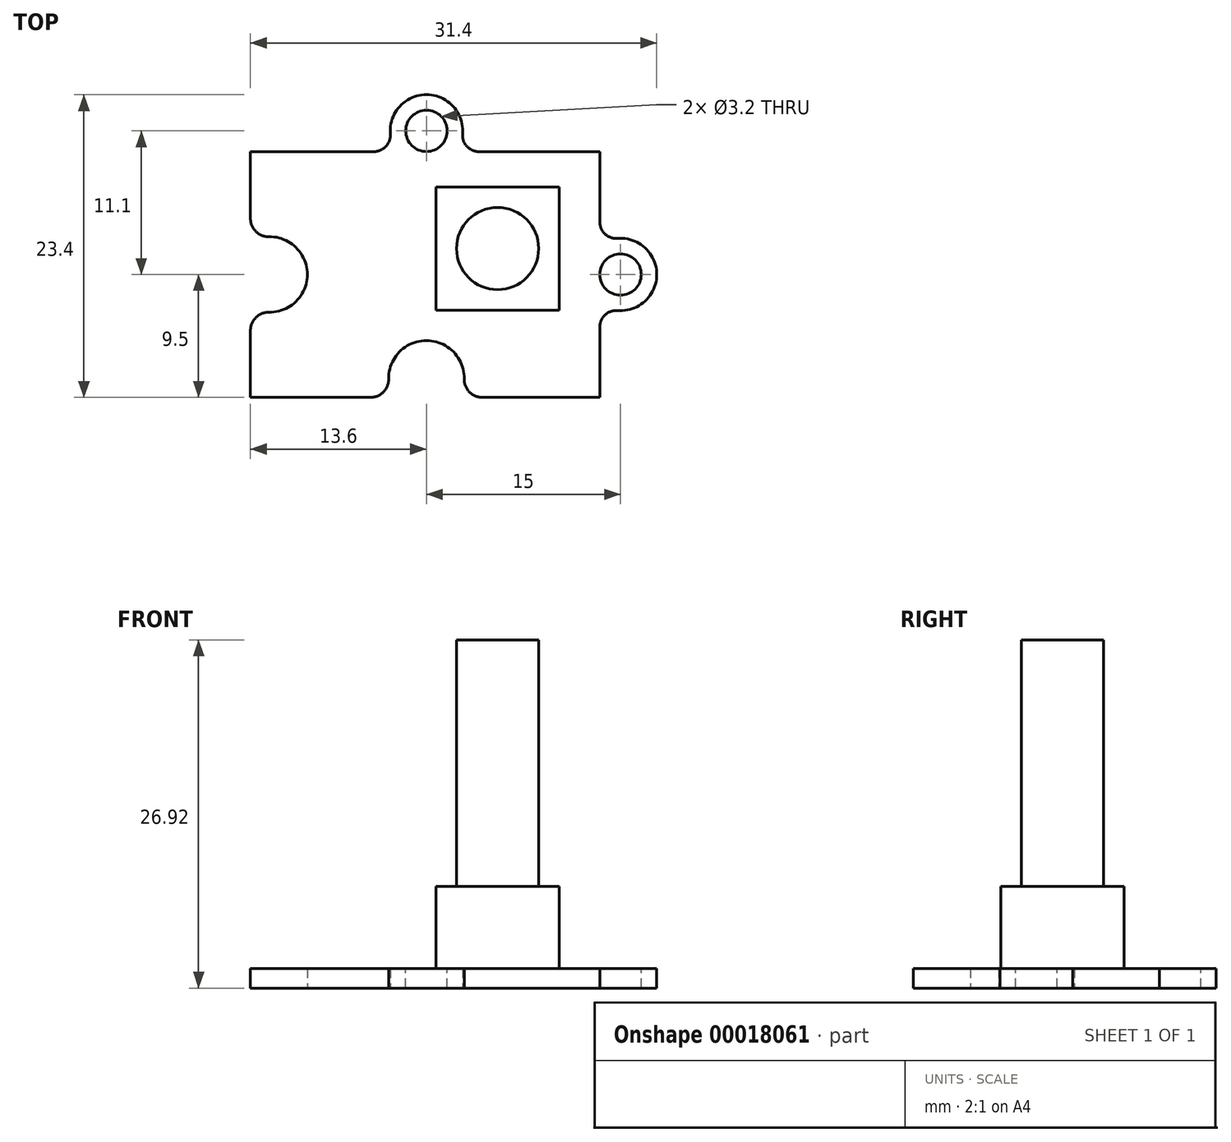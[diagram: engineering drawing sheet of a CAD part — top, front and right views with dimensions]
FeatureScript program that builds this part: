
annotation { "Feature Type Name" : "Feature", "Feature Type Description" : "" }
export const myFeature = defineFeature(function(context is Context, id is Id, definition is map)
    precondition{}
    {
        {
            var Q0;
            Q0=qCreatedBy(makeId("Top.planeOp"),FACE);
            var sketch = newSketch(context, id + "F0", { "sketchPlane" : qUnion([Q0])});
            skLineSegment(sketch, "E0.bottom", {"start": v(0, 0) * mm, "end": v(9.28, 0) * mm});
            skLineSegment(sketch, "E0.top", {"start": v(0, 19) * mm, "end": v(9.54, 19) * mm});
            skLineSegment(sketch, "E0.left", {"start": v(0, 0) * mm, "end": v(0, 5.18) * mm});
            skLineSegment(sketch, "E0.right", {"start": v(27, 0) * mm, "end": v(27, 5.44) * mm});
            skLineSegment(sketch, "E1", {"start": v(-7.73, 9.5) * mm, "end": v(31.46, 9.5) * mm, "construction": true});
            skPoint(sketch, "E2", {"position": v(0, 9.5) * mm});
            skPoint(sketch, "E3", {"position": v(27, 9.5) * mm});
            skArc(sketch, "E4", {"start": v(1.42, 6.58) * mm, "mid": v(4.4, 9.5) * mm, "end": v(1.42, 12.42) * mm});
            skArc(sketch, "E5", {"start": v(28.37, 6.7) * mm, "mid": v(31.4, 9.5) * mm, "end": v(28.37, 12.3) * mm});
            skLineSegment(sketch, "E6", {"start": v(13.6, 24.26) * mm, "end": v(13.6, -6.17) * mm, "construction": true});
            skArc(sketch, "E7", {"start": v(16.4, 20.37) * mm, "mid": v(13.6, 23.4) * mm, "end": v(10.8, 20.37) * mm});
            skArc(sketch, "E8", {"start": v(16.52, 1.42) * mm, "mid": v(13.6, 4.4) * mm, "end": v(10.68, 1.42) * mm});
            skCircle(sketch, "E9", {"center": v(13.6, 20.6) * mm, "radius": 1.6 * mm, "construction": true});
            skCircle(sketch, "E10", {"center": v(28.6, 9.5) * mm, "radius": 1.6 * mm, "construction": true});
            skLineSegment(sketch, "E11.trimOffspring", {"start": v(0, 13.82) * mm, "end": v(0, 19) * mm});
            skLineSegment(sketch, "E12.trimOffspring", {"start": v(27, 13.56) * mm, "end": v(27, 19) * mm});
            skLineSegment(sketch, "E13.trimOffspring", {"start": v(17.66, 19) * mm, "end": v(27, 19) * mm});
            skLineSegment(sketch, "E14.trimOffspring", {"start": v(17.92, 0) * mm, "end": v(27, 0) * mm});
            skPoint(sketch, "E15.visualSharp", {"position": v(11.3, 19) * mm});
            skArc(sketch, "E15.filletArc", {"start": v(9.54, 19) * mm, "mid": v(10.48, 19.4) * mm, "end": v(10.8, 20.37) * mm});
            skPoint(sketch, "E16.visualSharp", {"position": v(15.9, 19) * mm});
            skArc(sketch, "E16.filletArc", {"start": v(16.4, 20.37) * mm, "mid": v(16.72, 19.4) * mm, "end": v(17.66, 19) * mm});
            skPoint(sketch, "E17.visualSharp", {"position": v(11.08, 0) * mm});
            skArc(sketch, "E17.filletArc", {"start": v(9.28, 0) * mm, "mid": v(10.28, 0.42) * mm, "end": v(10.68, 1.42) * mm});
            skPoint(sketch, "E18.visualSharp", {"position": v(16.12, 0) * mm});
            skArc(sketch, "E18.filletArc", {"start": v(16.52, 1.42) * mm, "mid": v(16.92, 0.42) * mm, "end": v(17.92, 0) * mm});
            skPoint(sketch, "E19.visualSharp", {"position": v(27, 11.8) * mm});
            skArc(sketch, "E19.filletArc", {"start": v(27, 13.56) * mm, "mid": v(27.4, 12.62) * mm, "end": v(28.37, 12.3) * mm});
            skPoint(sketch, "E20.visualSharp", {"position": v(27, 7.2) * mm});
            skArc(sketch, "E20.filletArc", {"start": v(28.37, 6.7) * mm, "mid": v(27.4, 6.38) * mm, "end": v(27, 5.44) * mm});
            skPoint(sketch, "E21.visualSharp", {"position": v(0, 12.02) * mm});
            skArc(sketch, "E21.filletArc", {"start": v(0, 13.82) * mm, "mid": v(0.42, 12.82) * mm, "end": v(1.42, 12.42) * mm});
            skPoint(sketch, "E22.visualSharp", {"position": v(0, 6.98) * mm});
            skArc(sketch, "E22.filletArc", {"start": v(1.42, 6.58) * mm, "mid": v(0.42, 6.18) * mm, "end": v(0, 5.18) * mm});
            skSolve(sketch);
        }
        {
            var Q0;
            Q0 = qSketchRegion(id + "F0", true);
            extrude(context, id + "F1", {"entities" : qUnion([Q0]), "depth" : 1.52 * mm});
        }
        {
            var Q0;
            Q0=makeQuery(id+"F1.opExtrude","CAP_FACE",FACE,{"disambiguationData":[OSD([sQuery(id+"F0.wireOp",EDGE,"E0.bottom"),sQuery(id+"F0.wireOp",EDGE,"E0.top"),sQuery(id+"F0.wireOp",EDGE,"E0.left"),sQuery(id+"F0.wireOp",EDGE,"E0.right"),sQuery(id+"F0.wireOp",EDGE,"E4"),sQuery(id+"F0.wireOp",EDGE,"E5"),sQuery(id+"F0.wireOp",EDGE,"E7"),sQuery(id+"F0.wireOp",EDGE,"E8"),sQuery(id+"F0.wireOp",EDGE,"E11.trimOffspring"),sQuery(id+"F0.wireOp",EDGE,"E12.trimOffspring"),sQuery(id+"F0.wireOp",EDGE,"E13.trimOffspring"),sQuery(id+"F0.wireOp",EDGE,"E14.trimOffspring"),sQuery(id+"F0.wireOp",EDGE,"E15.filletArc"),sQuery(id+"F0.wireOp",EDGE,"E16.filletArc"),sQuery(id+"F0.wireOp",EDGE,"E17.filletArc"),sQuery(id+"F0.wireOp",EDGE,"E18.filletArc"),sQuery(id+"F0.wireOp",EDGE,"E19.filletArc"),sQuery(id+"F0.wireOp",EDGE,"E20.filletArc"),sQuery(id+"F0.wireOp",EDGE,"E21.filletArc"),sQuery(id+"F0.wireOp",EDGE,"E22.filletArc")])],"isStart":false});
            var sketch = newSketch(context, id + "F2", { "sketchPlane" : qUnion([Q0])});
            skCircle(sketch, "E23", {"center": v(19.1, 11.5) * mm, "radius": 3.05 * mm, "construction": true});
            skPoint(sketch, "E24", {"position": v(28.6, 9.5) * mm});
            skPoint(sketch, "E25", {"position": v(13.6, 20.6) * mm});
            skLineSegment(sketch, "E26.bottom", {"start": v(14.34, 16.27) * mm, "end": v(23.86, 16.27) * mm});
            skLineSegment(sketch, "E26.top", {"start": v(14.34, 6.74) * mm, "end": v(23.86, 6.74) * mm});
            skLineSegment(sketch, "E26.left", {"start": v(14.34, 16.27) * mm, "end": v(14.34, 6.74) * mm});
            skLineSegment(sketch, "E26.right", {"start": v(23.86, 16.27) * mm, "end": v(23.86, 6.74) * mm});
            skSolve(sketch);
        }
        {
            var Q0;
            Q0 = qSketchRegion(id + "F2", true);
            extrude(context, id + "F3", {"entities" : qUnion([Q0]), "operationType" : NewBodyOperationType.ADD, "depth" : 6.35 * mm});
        }
        {
            var Q0;
            Q0=makeQuery(id+"F3.opExtrude","CAP_FACE",FACE,{"disambiguationData":[OSD([sQuery(id+"F2.wireOp",EDGE,"E26.bottom"),sQuery(id+"F2.wireOp",EDGE,"E26.top"),sQuery(id+"F2.wireOp",EDGE,"E26.left"),sQuery(id+"F2.wireOp",EDGE,"E26.right")])],"isStart":false});
            var sketch = newSketch(context, id + "F4", { "sketchPlane" : qUnion([Q0])});
            skPoint(sketch, "E27.0", {"position": v(19.1, 11.5) * mm});
            skCircle(sketch, "E28", {"center": v(19.1, 11.5) * mm, "radius": 3.18 * mm});
            skSolve(sketch);
        }
        {
            var Q0;
            Q0 = qSketchRegion(id + "F4", true);
            extrude(context, id + "F5", {"entities" : qUnion([Q0]), "operationType" : NewBodyOperationType.ADD, "depth" : 19.05 * mm});
        }
        {
            var Q0;
            Q0=makeQuery(id+"F2.imprint","IMPRINT",FACE,{"disambiguationData":[TD([[makeQuery(id+"F2.imprint","IMPRINT",EDGE,{"derivedFrom":sQuery(id+"F2.wireOp",EDGE,"E26.bottom")}),1.0]])]});
            var sketch = newSketch(context, id + "F6", { "sketchPlane" : qUnion([Q0])});
            skCircle(sketch, "E29", {"center": v(13.6, 20.6) * mm, "radius": 1.6 * mm});
            skCircle(sketch, "E30", {"center": v(28.6, 9.5) * mm, "radius": 1.6 * mm});
            skSolve(sketch);
        }
        {
            var Q0;
            Q0 = qSketchRegion(id + "F6", true);
            var Q1;
            Q1=makeQuery(id+"F1.opExtrude","CAP_FACE",FACE,{"disambiguationData":[OSD([sQuery(id+"F0.wireOp",EDGE,"E0.bottom"),sQuery(id+"F0.wireOp",EDGE,"E0.top"),sQuery(id+"F0.wireOp",EDGE,"E0.left"),sQuery(id+"F0.wireOp",EDGE,"E0.right"),sQuery(id+"F0.wireOp",EDGE,"E4"),sQuery(id+"F0.wireOp",EDGE,"E5"),sQuery(id+"F0.wireOp",EDGE,"E7"),sQuery(id+"F0.wireOp",EDGE,"E8"),sQuery(id+"F0.wireOp",EDGE,"E11.trimOffspring"),sQuery(id+"F0.wireOp",EDGE,"E12.trimOffspring"),sQuery(id+"F0.wireOp",EDGE,"E13.trimOffspring"),sQuery(id+"F0.wireOp",EDGE,"E14.trimOffspring"),sQuery(id+"F0.wireOp",EDGE,"E15.filletArc"),sQuery(id+"F0.wireOp",EDGE,"E16.filletArc"),sQuery(id+"F0.wireOp",EDGE,"E17.filletArc"),sQuery(id+"F0.wireOp",EDGE,"E18.filletArc"),sQuery(id+"F0.wireOp",EDGE,"E19.filletArc"),sQuery(id+"F0.wireOp",EDGE,"E20.filletArc"),sQuery(id+"F0.wireOp",EDGE,"E21.filletArc"),sQuery(id+"F0.wireOp",EDGE,"E22.filletArc")])],"isStart":true});
            extrude(context, id + "F7", {"entities" : qUnion([Q0]), "operationType" : NewBodyOperationType.REMOVE, "endBound" : BoundingType.UP_TO_SURFACE, "oppositeDirection" : true, "endBoundEntityFace" : qUnion([Q1]), "depth" : 25.4 * mm});
        }
    });
